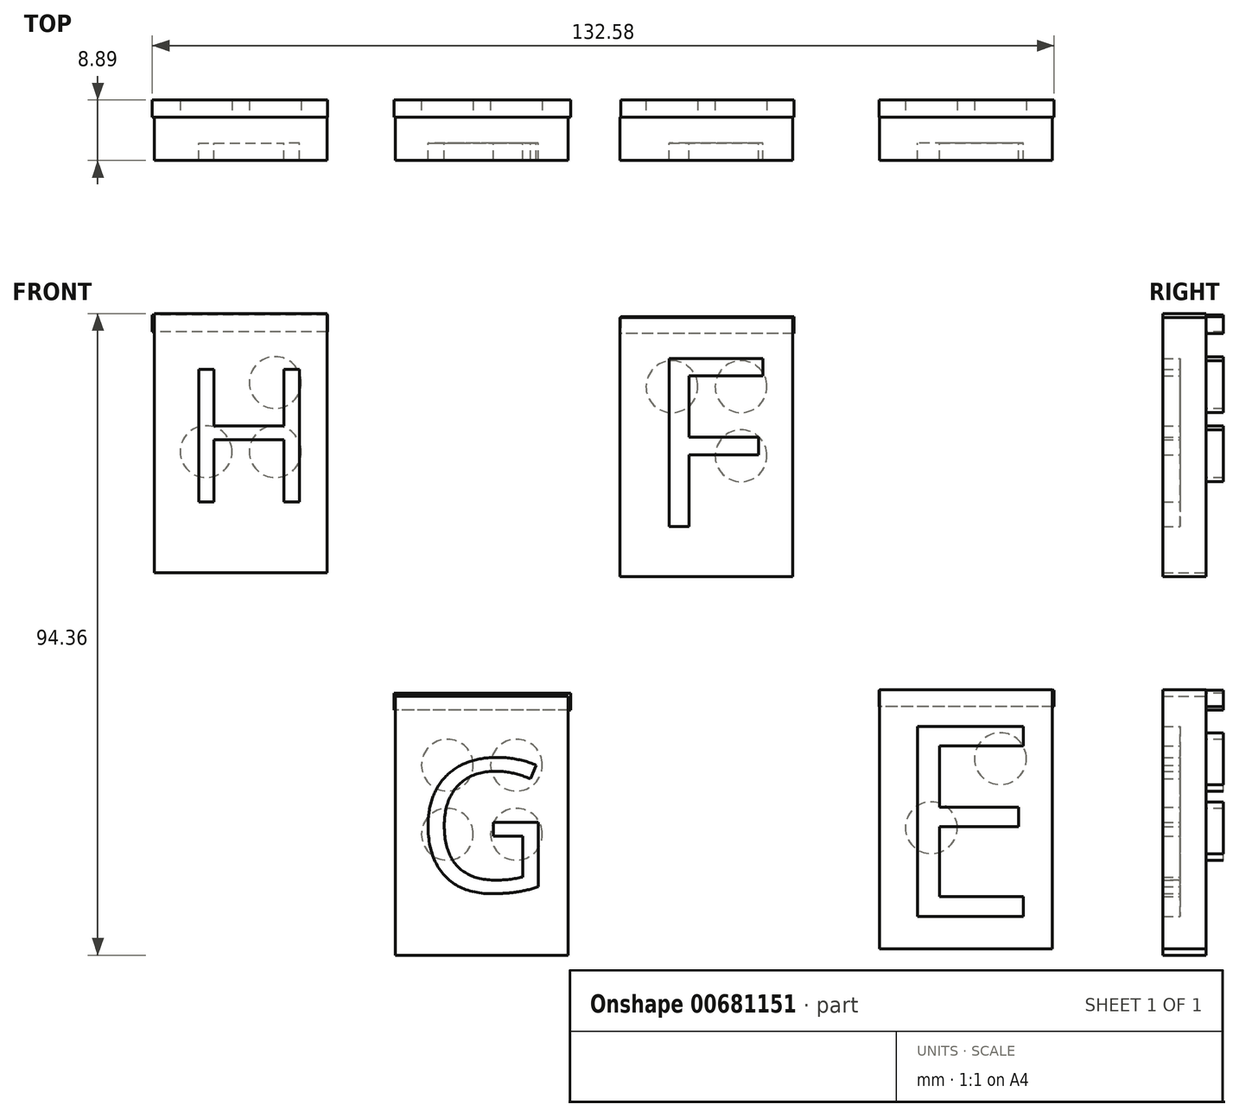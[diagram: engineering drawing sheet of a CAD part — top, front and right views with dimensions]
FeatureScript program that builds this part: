
annotation { "Feature Type Name" : "Feature", "Feature Type Description" : "" }
export const myFeature = defineFeature(function(context is Context, id is Id, definition is map)
    precondition{}
    {
        {
            var Q0;
            Q0=qCreatedBy(makeId("Front.planeOp"),FACE);
            var sketch = newSketch(context, id + "F0", { "sketchPlane" : qUnion([Q0])});
            skLineSegment(sketch, "E0.bottom", {"start": v(-58.76, 38.35) * mm, "end": v(-33.36, 38.35) * mm});
            skLineSegment(sketch, "E0.top", {"start": v(-58.76, 0.25) * mm, "end": v(-33.36, 0.25) * mm});
            skLineSegment(sketch, "E0.left", {"start": v(-58.76, 38.35) * mm, "end": v(-58.76, 0.25) * mm});
            skLineSegment(sketch, "E0.right", {"start": v(-33.36, 38.35) * mm, "end": v(-33.36, 0.25) * mm});
            skLineSegment(sketch, "E1.bottom", {"start": v(-23.3, -17.91) * mm, "end": v(2.1, -17.91) * mm});
            skLineSegment(sketch, "E1.top", {"start": v(-23.3, -56.01) * mm, "end": v(2.1, -56.01) * mm});
            skLineSegment(sketch, "E1.left", {"start": v(-23.3, -17.91) * mm, "end": v(-23.3, -56.01) * mm});
            skLineSegment(sketch, "E1.right", {"start": v(2.1, -17.91) * mm, "end": v(2.1, -56.01) * mm});
            skLineSegment(sketch, "E2.bottom", {"start": v(47.85, -16.96) * mm, "end": v(73.25, -16.96) * mm});
            skLineSegment(sketch, "E2.top", {"start": v(47.85, -55.06) * mm, "end": v(73.25, -55.06) * mm});
            skLineSegment(sketch, "E2.left", {"start": v(47.85, -16.96) * mm, "end": v(47.85, -55.06) * mm});
            skLineSegment(sketch, "E2.right", {"start": v(73.25, -16.96) * mm, "end": v(73.25, -55.06) * mm});
            skLineSegment(sketch, "E3.bottom", {"start": v(9.7, 37.75) * mm, "end": v(35.1, 37.75) * mm});
            skLineSegment(sketch, "E3.top", {"start": v(9.7, -0.35) * mm, "end": v(35.1, -0.35) * mm});
            skLineSegment(sketch, "E3.left", {"start": v(9.7, 37.75) * mm, "end": v(9.7, -0.35) * mm});
            skLineSegment(sketch, "E3.right", {"start": v(35.1, 37.75) * mm, "end": v(35.1, -0.35) * mm});
            skSolve(sketch);
        }
        {
            var Q0;
            Q0=qSketchRegion(id+"F0",true);
            extrude(context, id + "F1", {"entities" : qUnion([Q0]), "depth" : 6.35 * mm});
        }
        {
            var Q0;
            Q0=qCreatedBy(makeId("Front.planeOp"),FACE);
            var sketch = newSketch(context, id + "F2", { "sketchPlane" : qUnion([Q0])});
            skCircle(sketch, "E4", {"center": v(27.49, 17.43) * mm, "radius": 3.81 * mm});
            skCircle(sketch, "E5", {"center": v(65.63, -27.12) * mm, "radius": 3.81 * mm});
            skCircle(sketch, "E6", {"center": v(-5.52, -38.23) * mm, "radius": 3.81 * mm});
            skCircle(sketch, "E7", {"center": v(-15.68, -28.07) * mm, "radius": 3.81 * mm});
            skCircle(sketch, "E8", {"center": v(27.49, 27.59) * mm, "radius": 3.81 * mm});
            skCircle(sketch, "E9", {"center": v(17.33, 27.59) * mm, "radius": 3.81 * mm});
            skCircle(sketch, "E10", {"center": v(-5.52, -28.07) * mm, "radius": 3.8 * mm});
            skCircle(sketch, "E11", {"center": v(-40.98, 28.19) * mm, "radius": 3.81 * mm});
            skCircle(sketch, "E12", {"center": v(-51.14, 18.03) * mm, "radius": 3.81 * mm});
            skCircle(sketch, "E13", {"center": v(-40.98, 18.03) * mm, "radius": 3.81 * mm});
            skCircle(sketch, "E14", {"center": v(55.47, -37.28) * mm, "radius": 3.81 * mm});
            skCircle(sketch, "E15", {"center": v(-15.68, -38.23) * mm, "radius": 3.81 * mm});
            skSolve(sketch);
        }
        {
            var Q0;
            Q0=qSketchRegion(id+"F2",true);
            extrude(context, id + "F3", {"entities" : qUnion([Q0]), "operationType" : NewBodyOperationType.ADD, "oppositeDirection" : true, "depth" : 2.54 * mm});
        }
        {
            var Q0;
            Q0=qCreatedBy(makeId("Front.planeOp"),FACE);
            cPlane(context, id + "F4", {"entities" : qUnion([Q0]), "cplaneType" : CPlaneType.OFFSET, "offset" : 3.8 * mm, "width" : 152.4 * mm, "height" : 152.4 * mm});
        }
        {
            var Q0;
            Q0=qCreatedBy(id+"F4.planeOp",FACE);
            var sketch = newSketch(context, id + "F5", { "sketchPlane" : qUnion([Q0])});
            skText(sketch, "E16", { "text": "E", "fontName": "OpenSans-Regular.ttf"});
            skText(sketch, "E17", { "text": "F", "fontName": "OpenSans-Regular.ttf"});
            skText(sketch, "E18", { "text": "G", "fontName": "OpenSans-Regular.ttf"});
            skText(sketch, "E19", { "text": "H", "fontName": "OpenSans-Regular.ttf"});
            const initialGuessF5  = {"E16": [0.0496, -0.0503, 1, 0, 0.02818], "E17": [0.01356, 0.00704, 1, 0, 0.0249], "E18": [-0.02019, -0.0467, 1, 0, 0.01966], "E19": [-0.05492, 0.01064, 1, 0, 0.01966]};
            skSetInitialGuess(sketch, initialGuessF5);
            skSolve(sketch);
        }
        {
            var Q0;
            Q0=qSketchRegion(id+"F5",true);
            extrude(context, id + "F6", {"entities" : qUnion([Q0]), "operationType" : NewBodyOperationType.REMOVE, "depth" : 25.4 * mm});
        }
        {
            var Q0;
            Q0=qCreatedBy(makeId("Front.planeOp"),FACE);
            var sketch = newSketch(context, id + "F7", { "sketchPlane" : qUnion([Q0])});
            skLineSegment(sketch, "E20.bottom", {"start": v(73.52, -17.03) * mm, "end": v(47.79, -17.03) * mm});
            skLineSegment(sketch, "E20.top", {"start": v(73.52, -19.48) * mm, "end": v(47.79, -19.48) * mm});
            skLineSegment(sketch, "E20.left", {"start": v(73.52, -17.03) * mm, "end": v(73.52, -19.48) * mm});
            skLineSegment(sketch, "E20.right", {"start": v(47.79, -17.03) * mm, "end": v(47.79, -19.48) * mm});
            skLineSegment(sketch, "E21.bottom", {"start": v(35.29, 37.86) * mm, "end": v(9.8, 37.86) * mm});
            skLineSegment(sketch, "E21.top", {"start": v(35.29, 35.41) * mm, "end": v(9.8, 35.41) * mm});
            skLineSegment(sketch, "E21.left", {"start": v(35.29, 37.86) * mm, "end": v(35.29, 35.41) * mm});
            skLineSegment(sketch, "E21.right", {"start": v(9.8, 37.86) * mm, "end": v(9.8, 35.41) * mm});
            skLineSegment(sketch, "E22.bottom", {"start": v(-33.33, 38.1) * mm, "end": v(-59.06, 38.1) * mm});
            skLineSegment(sketch, "E22.top", {"start": v(-33.33, 35.66) * mm, "end": v(-59.06, 35.66) * mm});
            skLineSegment(sketch, "E22.left", {"start": v(-33.33, 38.1) * mm, "end": v(-33.33, 35.66) * mm});
            skLineSegment(sketch, "E22.right", {"start": v(-59.06, 38.1) * mm, "end": v(-59.06, 35.66) * mm});
            skLineSegment(sketch, "E23.bottom", {"start": v(2.45, -17.52) * mm, "end": v(-23.53, -17.52) * mm});
            skLineSegment(sketch, "E23.top", {"start": v(2.45, -19.97) * mm, "end": v(-23.53, -19.97) * mm});
            skLineSegment(sketch, "E23.left", {"start": v(2.45, -17.52) * mm, "end": v(2.45, -19.97) * mm});
            skLineSegment(sketch, "E23.right", {"start": v(-23.53, -17.52) * mm, "end": v(-23.53, -19.97) * mm});
            skSolve(sketch);
        }
        {
            var Q0;
            Q0=qSketchRegion(id+"F7",true);
            extrude(context, id + "F8", {"entities" : qUnion([Q0]), "operationType" : NewBodyOperationType.ADD, "oppositeDirection" : true, "depth" : 2.54 * mm});
        }
    });
